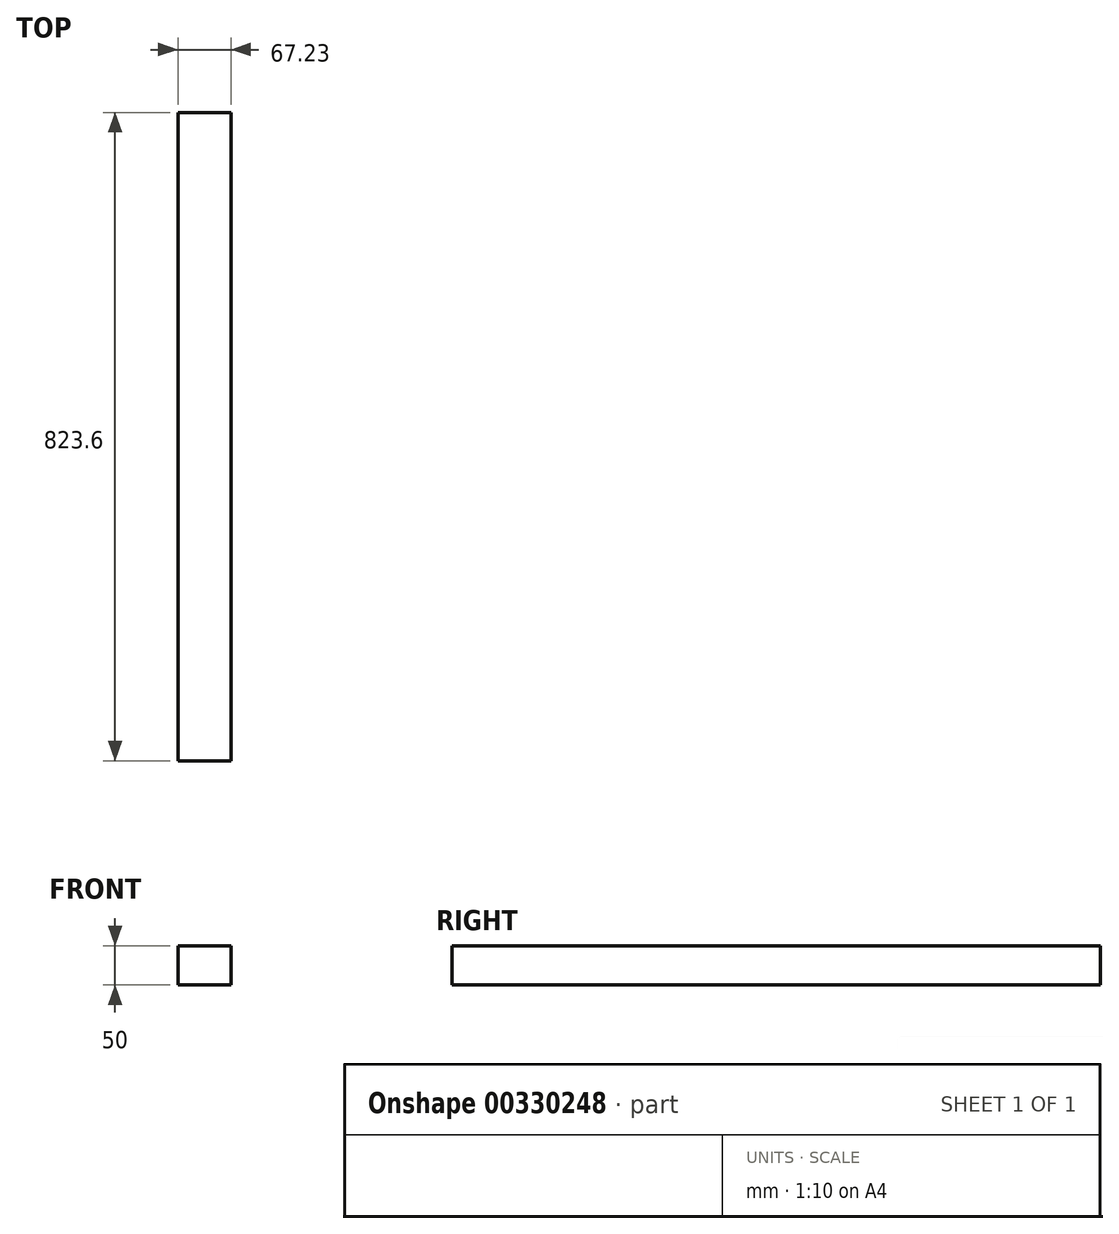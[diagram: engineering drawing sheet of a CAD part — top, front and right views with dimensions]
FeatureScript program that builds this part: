
annotation { "Feature Type Name" : "Feature", "Feature Type Description" : "" }
export const myFeature = defineFeature(function(context is Context, id is Id, definition is map)
    precondition{}
    {
        {
            var Q0;
            Q0=qCreatedBy(makeId("Top.planeOp"),FACE);
            var sketch = newSketch(context, id + "F0", { "sketchPlane" : qUnion([Q0])});
            skLineSegment(sketch, "E0.bottom", {"start": v(-67.23, 0) * mm, "end": v(0, 0) * mm});
            skLineSegment(sketch, "E0.top", {"start": v(-67.23, -823.6) * mm, "end": v(0, -823.6) * mm});
            skLineSegment(sketch, "E0.left", {"start": v(-67.23, 0) * mm, "end": v(-67.23, -823.6) * mm});
            skLineSegment(sketch, "E0.right", {"start": v(0, 0) * mm, "end": v(0, -823.6) * mm});
            skSolve(sketch);
        }
        {
            var Q0;
            Q0 = qSketchRegion(id + "F0", true);
            extrude(context, id + "F1", {"entities" : qUnion([Q0]), "depth" : 50 * mm});
        }
    });
